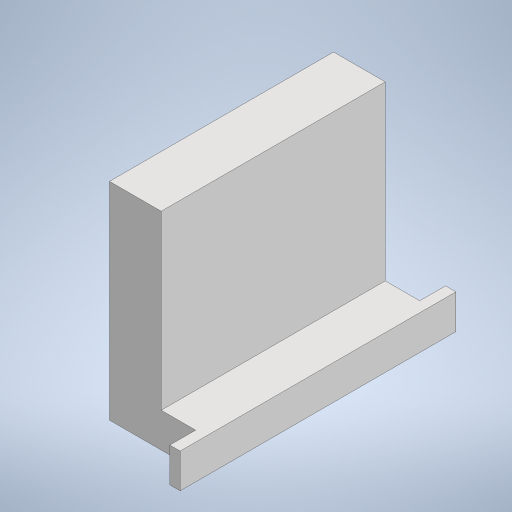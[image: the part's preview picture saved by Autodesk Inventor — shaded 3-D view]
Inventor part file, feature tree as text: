
AUTODESK INVENTOR PART (.ipt)
format: ipt  version: 2024 (Build 280153000, 153)  size: 223,744 bytes
history: native  units: mm
features: extrude x4, sketch x4
ambient origin geometry x8: Origin, YZ Plane, XZ Plane, XY Plane, X Axis, Y Axis, Z Axis, Center Point
bodies: Solid1 (feature_tree)
feature tree (8):
  extrude  "Extrusion1"  Depth=160.0mm
  extrude  "Extrusion2"  Depth=15.0mm
  extrude  "Extrusion3"  Depth=20.0mm
  extrude  "Extrusion4"  Depth=30.0mm
  sketch  "Sketch1"  dims[d0=6.0mm d1=160.0mm]
  sketch  "Sketch2"  dims[d2=20.0mm d3=0.0mm d4=15.0mm]
  sketch  "Sketch3"  dims[d5=15.0mm d6=20.0mm]
  sketch  "Sketch4"  dims[d7=50.0mm d8=0.0mm d9=30.0mm d10=100.0mm d11=0.0mm d12=16.0mm d13=50.0mm d14=50.0mm d15=0.0mm]
